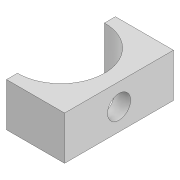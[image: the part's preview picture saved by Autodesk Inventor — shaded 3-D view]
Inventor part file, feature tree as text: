
AUTODESK INVENTOR PART (.ipt)
format: ipt  version: 2022 (Build 260153000, 153)  size: 102,400 bytes
history: native  units: mm
features: extrude x2, sketch x2
ambient origin geometry x8: Origin, YZ Plane, XZ Plane, XY Plane, X Axis, Y Axis, Z Axis, Center Point
bodies: Solid1 (feature_tree)
feature tree (4):
  extrude  "Extrusion1"  Depth=6.0mm TaperAngle=0.0deg
  extrude  "Extrusion2"  Depth=6.0mm
  sketch  "Sketch1"  dims[d1=8.0mm d2=6.0mm d3=0.0mm]
  sketch  "Sketch2"  dims[d4=3.2mm d5=3.0mm d6=7.5mm d7=15.0mm d8=15.0mm d9=12.0mm d10=6.0mm d11=0.0mm]
